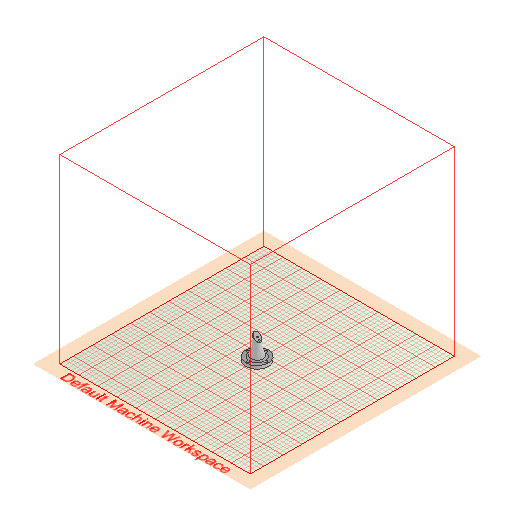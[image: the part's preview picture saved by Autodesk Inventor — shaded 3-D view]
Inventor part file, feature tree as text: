
AUTODESK INVENTOR PART (.ipt)
format: ipt  version: 2022 (Build 260153000, 153)  size: 481,792 bytes
history: native  units: mm
features: sketch x9, extrude x6, projected_geometry x5, revolve x1, plane x1, fillet x1, other x1
ambient origin geometry x8: Origin, YZ Plane, XZ Plane, XY Plane, X Axis, Y Axis, Z Axis, Center Point
bodies: Solid1 (feature_tree)
feature tree (24):
  extrude  "Extrusion1"  Depth=7.0mm TaperAngle=0.0deg
  sketch  "Sketch2"  dims[d9=15.0mm d11=7.0mm]
  revolve  "Revolution1"  [1 undecoded]
  sketch  "Sketch4"  dims[d14=37.0mm d16=45.0deg]
  plane  "Work Plane1"
  extrude  "Extrusion2"  Depth=73.0mm
  extrude  "Extrusion3"  TaperAngle=45.0deg  [1 undecoded]
  extrude  "Extrusion4"  Depth=10.0mm TaperAngle=0.0deg
  extrude  "Extrusion5"  Depth=20.0mm
  extrude  "Extrusion6"  Depth=3.0mm
  fillet  "Fillet1"  Radius=3.0mm
  sketch  "Sketch1"  dims[d1=30.0mm d2=20.0mm d3=90.0deg d4=6.0mm d5=90.0deg d6=135.0deg d7=7.0mm d8=0.0mm]
  sketch  "Sketch3"  dims[d12=360.0deg d13=73.0mm]
  other  "Work Axis1"
  sketch  "Sketch5"  dims[d17=10.0mm d18=0.0mm d19=10.0mm d20=0.0mm]
  projected_geometry  "Projected Loop1"
  sketch  "Sketch6"  dims[d21=40.0mm d22=20.0mm]
  projected_geometry  "Projected Loop2"
  sketch  "Sketch7"  dims[d23=0.0mm d24=3.0mm d25=3.0mm]
  projected_geometry  "Projected Loop3"
  sketch  "Sketch8"  dims[d26=3.0mm]
  projected_geometry  "Projected Loop4"
  sketch  "Sketch9"  dims[d27=4.0mm d28=6.0mm d29=5.0mm d30=0.0mm d31=3.0mm d32=0.0mm d33=1.0mm d34=0.0mm d35=4.0mm d36=0.0mm d37=0.0mm d38=0.0mm]
  projected_geometry  "Projected Loop5"
note: 2 required parameter values undecoded (feature->parameter linkage not recoverable at this tier; creation-order binding heuristic only, values carry confidence <= 0.55)